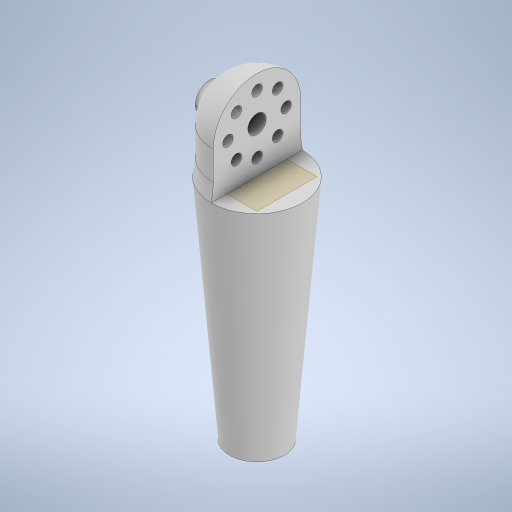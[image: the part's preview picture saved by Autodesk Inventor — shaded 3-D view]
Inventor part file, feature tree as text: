
AUTODESK INVENTOR PART (.ipt)
format: ipt  version: 2024 (Build 280153000, 153)  size: 769,024 bytes
history: native  units: in
note: dims shown in document units (in); Inventor stores cm internally (conversion verified against a paired STEP export)
features: sketch x7, extrude x5, fillet x3, plane x2, loft x1, thicken_offset x1
ambient origin geometry x8: Origin, YZ Plane, XZ Plane, XY Plane, X Axis, Y Axis, Z Axis, Center Point
bodies: Solid1 (feature_tree)
feature tree (19):
  sketch  "Sketch1"  dims[d0=0.6in d2=2.5in]
  plane  "Work Plane1"
  loft  "Loft1"
  extrude  "Extrusion1"  TaperAngle=0.0deg  [1 undecoded]
  extrude  "Extrusion2"  Depth=1.0in TaperAngle=0.0deg
  fillet  "Fillet2"  Radius=0.115in
  extrude  "Extrusion3"  Depth=0.105in TaperAngle=0.0deg
  thicken_offset  "Thicken1"
  plane  "Work Plane2"
  extrude  "Extrusion4"  Depth=0.5in
  extrude  "Extrusion5"  [1 undecoded]
  fillet  "Fillet4"  Radius=0.315in
  fillet  "Fillet5"  Radius=0.08in
  sketch  "Sketch2"  dims[d3=1.0in d4=0.0in d5=90.0deg]
  sketch  "Sketch3"  dims[d6=0.0in d7=90.0deg d8=1.0in d9=0.0in d12=0.115in]
  sketch  "Sketch4"  dims[d13=3.1496in d15=360.0deg d17=0.105in d18=0.0in]
  sketch  "Sketch5"  dims[d20=0.5in d21=0.2in]
  sketch  "Sketch6"  dims[d22=1.0in d23=0.0in d24=-0.48in d25=0.315in d26=0.08in d27=0.0in]
  sketch  "Sketch7"  dims[d29=0.4126in d30=2.0in d31=0.0in d33=0.02in d34=0.02in d35=0.125in d36=0.875in]
note: 2 required parameter values undecoded (feature->parameter linkage not recoverable at this tier; creation-order binding heuristic only, values carry confidence <= 0.55)
